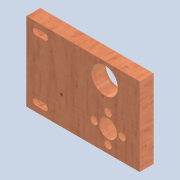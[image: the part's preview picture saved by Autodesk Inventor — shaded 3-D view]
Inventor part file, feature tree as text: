
AUTODESK INVENTOR PART (.ipt)
format: ipt  version: 2020 (Build 240168000, 168)  size: 315,904 bytes
history: native  units: mm
features: extrude x4, sketch x4, projected_geometry x1
ambient origin geometry x8: Origin, YZ Plane, XZ Plane, XY Plane, X Axis, Y Axis, Z Axis, Center Point
bodies: Solid1 (feature_tree)
feature tree (9):
  extrude  "Extrusion1"  Depth=45.0mm
  extrude  "Extrusion3"  Depth=8.0mm
  extrude  "Extrusion4"  Depth=3.5mm
  extrude  "Extrusion5"  TaperAngle=0.0deg  [1 undecoded]
  sketch  "Sketch1"  dims[d0=65.0mm d1=45.0mm]
  sketch  "Sketch3"  dims[d2=8.0mm d3=0.0mm d8=5.0mm]
  projected_geometry  "Projected Loop1"
  sketch  "Sketch4"  dims[d9=3.5mm d10=5.0mm]
  sketch  "Sketch5"  dims[d12=0.0mm d13=0.0mm d14=0.0mm d15=0.0mm d16=5.0mm d17=8.0mm d18=5.0mm d19=8.0mm d20=10.2mm d21=4.1mm d22=4.1mm d23=4.1mm d24=4.1mm d25=22.0mm d26=18.139532mm d27=8.0mm d28=8.0mm d29=8.0mm d30=12.5mm d31=15.0mm d32=23.0mm d33=20.0mm d34=10.0mm d35=0.0mm]
note: 1 required parameter value undecoded (feature->parameter linkage not recoverable at this tier; creation-order binding heuristic only, values carry confidence <= 0.55)
